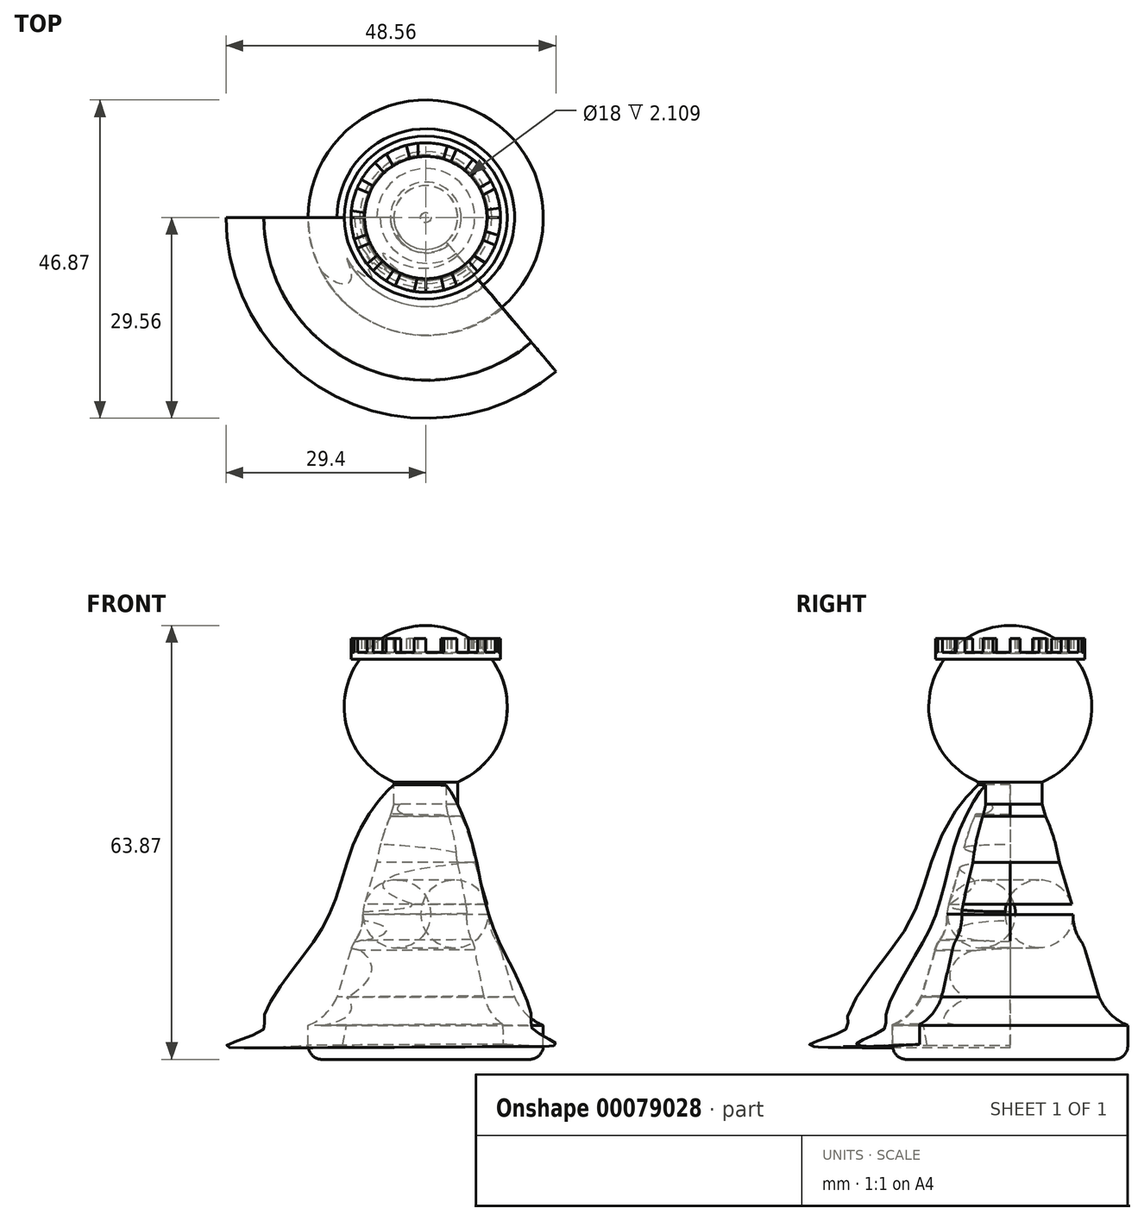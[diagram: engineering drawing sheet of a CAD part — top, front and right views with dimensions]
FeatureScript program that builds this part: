
annotation { "Feature Type Name" : "Feature", "Feature Type Description" : "" }
export const myFeature = defineFeature(function(context is Context, id is Id, definition is map)
    precondition{}
    {
        {
            var Q0;
            Q0=qCreatedBy(makeId("Front.planeOp"),FACE);
            var sketch = newSketch(context, id + "F0", { "sketchPlane" : qUnion([Q0])});
            skArc(sketch, "E0", {"start": v(0, 32.95) * mm, "mid": v(-11.76, 23.35) * mm, "end": v(-4.7, 9.9) * mm});
            skLineSegment(sketch, "E1", {"start": v(-4.7, 9.9) * mm, "end": v(-4.7, 6.63) * mm});
            skLineSegment(sketch, "E2", {"start": v(-4.7, 6.63) * mm, "end": v(-5.22, 4.84) * mm});
            skLineSegment(sketch, "E3", {"start": v(-14.3, -25.92) * mm, "end": v(0, -25.92) * mm});
            skLineSegment(sketch, "E4", {"start": v(0, -25.92) * mm, "end": v(0, 8.95) * mm});
            skArc(sketch, "E5", {"start": v(-10.38, -13.48) * mm, "mid": v(-9.51, -11.62) * mm, "end": v(-9.24, -9.6) * mm});
            skLineSegment(sketch, "E6.trimOffspring", {"start": v(-11.03, -14.85) * mm, "end": v(-13.07, -21.75) * mm});
            skPoint(sketch, "E7.visualSharp", {"position": v(-9.28, -8.93) * mm});
            skArc(sketch, "E7.filletArc", {"start": v(-9.03, -8.08) * mm, "mid": v(-9.2, -8.83) * mm, "end": v(-9.24, -9.6) * mm});
            skPoint(sketch, "E8.visualSharp", {"position": v(-10.78, -14) * mm});
            skArc(sketch, "E8.filletArc", {"start": v(-10.38, -13.48) * mm, "mid": v(-10.76, -14.14) * mm, "end": v(-11.03, -14.85) * mm});
            skLineSegment(sketch, "E9", {"start": v(0, 32.95) * mm, "end": v(0, 8.95) * mm});
            skArc(sketch, "E10", {"start": v(-17.3, -25.92) * mm, "mid": v(-14.78, -24.25) * mm, "end": v(-13.07, -21.75) * mm});
            skLineSegment(sketch, "E11", {"start": v(-17.3, -25.92) * mm, "end": v(-14.3, -25.92) * mm});
            skArc(sketch, "E12", {"start": v(-5.22, 4.84) * mm, "mid": v(-6.44, 1.54) * mm, "end": v(-7.2, -1.9) * mm});
            skLineSegment(sketch, "E13.trimOffspring", {"start": v(-7.2, -1.9) * mm, "end": v(-9.03, -8.08) * mm});
            skSolve(sketch);
        }
        {
            var Q0;
            Q0 = qSketchRegion(id + "F0", true);
            var Q1;
            Q1=sQuery(id+"F0.wireOp",EDGE,"E9");
            revolve(context, id + "F1", {"entities" : qUnion([Q0]), "axis" : qUnion([Q1]), "revolveType" : RevolveType.FULL});
        }
        {
            var Q0;
            Q0=qCreatedBy(makeId("Top.planeOp"),FACE);
            cPlane(context, id + "F2", {"entities" : qUnion([Q0]), "cplaneType" : CPlaneType.OFFSET, "offset" : 28 * mm, "width" : 150 * mm, "height" : 150 * mm});
        }
        {
            var Q0;
            Q0=qCreatedBy(id+"F2.planeOp",FACE);
            var sketch = newSketch(context, id + "F3", { "sketchPlane" : qUnion([Q0])});
            skCircle(sketch, "E14", {"center": v(0, 0) * mm, "radius": 11 * mm});
            skCircle(sketch, "E15", {"center": v(0, 0) * mm, "radius": 9 * mm});
            skLineSegment(sketch, "E16", {"start": v(-2.83, 10.63) * mm, "end": v(-2.32, 8.7) * mm});
            skLineSegment(sketch, "E17", {"start": v(-4.8, 7.61) * mm, "end": v(-5.8, 9.35) * mm});
            skLineSegment(sketch, "E18", {"start": v(-7.73, 4.6) * mm, "end": v(-9.47, 5.6) * mm});
            skLineSegment(sketch, "E19", {"start": v(9, 0) * mm, "end": v(11, 0) * mm});
            skLineSegment(sketch, "E20", {"start": v(6.29, -6.44) * mm, "end": v(7.6, -7.95) * mm});
            skLineSegment(sketch, "E21", {"start": v(3.82, -8.15) * mm, "end": v(4.57, -10) * mm});
            skLineSegment(sketch, "E22", {"start": v(2.25, -8.71) * mm, "end": v(2.66, -10.67) * mm});
            skLineSegment(sketch, "E23", {"start": v(0, -9) * mm, "end": v(0, -11) * mm});
            skLineSegment(sketch, "E24", {"start": v(-1.12, 10.94) * mm, "end": v(-1.12, 8.93) * mm});
            skLineSegment(sketch, "E25", {"start": v(-7.47, 8.08) * mm, "end": v(-6.1, 6.62) * mm});
            skLineSegment(sketch, "E26", {"start": v(-1.28, -8.9) * mm, "end": v(-1.7, -10.87) * mm});
            skLineSegment(sketch, "E27", {"start": v(-3.65, -8.22) * mm, "end": v(-4.5, -10.04) * mm});
            skLineSegment(sketch, "E28", {"start": v(-4.69, -7.68) * mm, "end": v(-5.84, -9.32) * mm});
            skLineSegment(sketch, "E29", {"start": v(-6.34, -6.39) * mm, "end": v(-7.74, -7.82) * mm});
            skLineSegment(sketch, "E30", {"start": v(-7.08, -5.55) * mm, "end": v(-8.66, -6.78) * mm});
            skLineSegment(sketch, "E31", {"start": v(-8.19, -3.74) * mm, "end": v(-10.03, -4.52) * mm});
            skLineSegment(sketch, "E32", {"start": v(-8.65, -2.5) * mm, "end": v(-10.54, -3.15) * mm});
            skLineSegment(sketch, "E33", {"start": v(-9, 0) * mm, "end": v(-11, 0) * mm});
            skLineSegment(sketch, "E34", {"start": v(-8.97, 0.69) * mm, "end": v(-10.95, 1.02) * mm});
            skLineSegment(sketch, "E35", {"start": v(-8.26, 3.57) * mm, "end": v(-10.12, 4.3) * mm});
            skLineSegment(sketch, "E36", {"start": v(7.07, -5.56) * mm, "end": v(8.75, -6.67) * mm});
            skLineSegment(sketch, "E37", {"start": v(8.37, -3.32) * mm, "end": v(10.23, -4.04) * mm});
            skLineSegment(sketch, "E38", {"start": v(8.77, -2.02) * mm, "end": v(10.7, -2.59) * mm});
            skLineSegment(sketch, "E39", {"start": v(8.93, 1.13) * mm, "end": v(10.9, 1.42) * mm});
            skLineSegment(sketch, "E40", {"start": v(8.38, 3.28) * mm, "end": v(10.15, 4.23) * mm});
            skLineSegment(sketch, "E41", {"start": v(7.86, 4.38) * mm, "end": v(9.62, 5.33) * mm});
            skLineSegment(sketch, "E42", {"start": v(6.65, 6.07) * mm, "end": v(8.07, 7.48) * mm});
            skLineSegment(sketch, "E43", {"start": v(5.74, 6.93) * mm, "end": v(6.92, 8.55) * mm});
            skLineSegment(sketch, "E44", {"start": v(3.67, 8.22) * mm, "end": v(4.51, 10.03) * mm});
            skLineSegment(sketch, "E45", {"start": v(2.58, 8.62) * mm, "end": v(3.2, 10.52) * mm});
            skSolve(sketch);
        }
        {
            var Q0;
            {var subQ0=sQuery(id+"F3.wireOp",EDGE,"E18");Q0=makeQuery(id+"F3.imprint","IMPRINT",FACE,{"disambiguationData":[TD([[makeQuery(id+"F3.imprint","IMPRINT",EDGE,{"derivedFrom":subQ0}),1.0]])]});}
            var Q1;
            {var subQ0=sQuery(id+"F3.wireOp",EDGE,"E17");Q1=makeQuery(id+"F3.imprint","IMPRINT",FACE,{"disambiguationData":[TD([[makeQuery(id+"F3.imprint","IMPRINT",EDGE,{"derivedFrom":subQ0}),1.0]])]});}
            var Q2;
            {var subQ0=sQuery(id+"F3.wireOp",EDGE,"E16");Q2=makeQuery(id+"F3.imprint","IMPRINT",FACE,{"disambiguationData":[TD([[makeQuery(id+"F3.imprint","IMPRINT",EDGE,{"derivedFrom":subQ0}),1.0]])]});}
            var Q3;
            {var subQ0=sQuery(id+"F3.wireOp",EDGE,"E44");Q3=makeQuery(id+"F3.imprint","IMPRINT",FACE,{"disambiguationData":[TD([[makeQuery(id+"F3.imprint","IMPRINT",EDGE,{"derivedFrom":subQ0}),1.0]])]});}
            var Q4;
            {var subQ0=sQuery(id+"F3.wireOp",EDGE,"E42");Q4=makeQuery(id+"F3.imprint","IMPRINT",FACE,{"disambiguationData":[TD([[makeQuery(id+"F3.imprint","IMPRINT",EDGE,{"derivedFrom":subQ0}),1.0]])]});}
            var Q5;
            {var subQ0=sQuery(id+"F3.wireOp",EDGE,"E40");Q5=makeQuery(id+"F3.imprint","IMPRINT",FACE,{"disambiguationData":[TD([[makeQuery(id+"F3.imprint","IMPRINT",EDGE,{"derivedFrom":subQ0}),1.0]])]});}
            var Q6;
            {var subQ0=sQuery(id+"F3.wireOp",EDGE,"E19");Q6=makeQuery(id+"F3.imprint","IMPRINT",FACE,{"disambiguationData":[TD([[makeQuery(id+"F3.imprint","IMPRINT",EDGE,{"derivedFrom":subQ0}),1.0]])]});}
            var Q7;
            {var subQ0=sQuery(id+"F3.wireOp",EDGE,"E37");Q7=makeQuery(id+"F3.imprint","IMPRINT",FACE,{"disambiguationData":[TD([[makeQuery(id+"F3.imprint","IMPRINT",EDGE,{"derivedFrom":subQ0}),1.0]])]});}
            var Q8;
            {var subQ0=sQuery(id+"F3.wireOp",EDGE,"E20");Q8=makeQuery(id+"F3.imprint","IMPRINT",FACE,{"disambiguationData":[TD([[makeQuery(id+"F3.imprint","IMPRINT",EDGE,{"derivedFrom":subQ0}),1.0]])]});}
            var Q9;
            {var subQ0=sQuery(id+"F3.wireOp",EDGE,"E21");Q9=makeQuery(id+"F3.imprint","IMPRINT",FACE,{"disambiguationData":[TD([[makeQuery(id+"F3.imprint","IMPRINT",EDGE,{"derivedFrom":subQ0}),-1.0]])]});}
            var Q10;
            {var subQ0=sQuery(id+"F3.wireOp",EDGE,"E23");Q10=makeQuery(id+"F3.imprint","IMPRINT",FACE,{"disambiguationData":[TD([[makeQuery(id+"F3.imprint","IMPRINT",EDGE,{"derivedFrom":subQ0}),-1.0]])]});}
            var Q11;
            {var subQ0=sQuery(id+"F3.wireOp",EDGE,"E27");Q11=makeQuery(id+"F3.imprint","IMPRINT",FACE,{"disambiguationData":[TD([[makeQuery(id+"F3.imprint","IMPRINT",EDGE,{"derivedFrom":subQ0}),-1.0]])]});}
            var Q12;
            {var subQ0=sQuery(id+"F3.wireOp",EDGE,"E29");Q12=makeQuery(id+"F3.imprint","IMPRINT",FACE,{"disambiguationData":[TD([[makeQuery(id+"F3.imprint","IMPRINT",EDGE,{"derivedFrom":subQ0}),-1.0]])]});}
            var Q13;
            {var subQ0=sQuery(id+"F3.wireOp",EDGE,"E31");Q13=makeQuery(id+"F3.imprint","IMPRINT",FACE,{"disambiguationData":[TD([[makeQuery(id+"F3.imprint","IMPRINT",EDGE,{"derivedFrom":subQ0}),-1.0]])]});}
            var Q14;
            {var subQ0=sQuery(id+"F3.wireOp",EDGE,"E33");Q14=makeQuery(id+"F3.imprint","IMPRINT",FACE,{"disambiguationData":[TD([[makeQuery(id+"F3.imprint","IMPRINT",EDGE,{"derivedFrom":subQ0}),-1.0]])]});}
            extrude(context, id + "F4", {"entities" : qUnion([Q0, Q1, Q2, Q3, Q4, Q5, Q6, Q7, Q8, Q9, Q10, Q11, Q12, Q13, Q14]), "operationType" : NewBodyOperationType.ADD, "depth" : 3 * mm});
        }
        {
            var Q0;
            {var subQ0=sQuery(id+"F3.wireOp",EDGE,"E16");Q0=makeQuery(id+"F3.imprint","IMPRINT",FACE,{"disambiguationData":[TD([[makeQuery(id+"F3.imprint","IMPRINT",EDGE,{"derivedFrom":subQ0}),-1.0]])]});}
            var Q1;
            {var subQ0=sQuery(id+"F3.wireOp",EDGE,"E18");Q1=makeQuery(id+"F3.imprint","IMPRINT",FACE,{"disambiguationData":[TD([[makeQuery(id+"F3.imprint","IMPRINT",EDGE,{"derivedFrom":subQ0}),-1.0]])]});}
            var Q2;
            {var subQ0=sQuery(id+"F3.wireOp",EDGE,"E34");Q2=makeQuery(id+"F3.imprint","IMPRINT",FACE,{"disambiguationData":[TD([[makeQuery(id+"F3.imprint","IMPRINT",EDGE,{"derivedFrom":subQ0}),-1.0]])]});}
            var Q3;
            {var subQ0=sQuery(id+"F3.wireOp",EDGE,"E32");Q3=makeQuery(id+"F3.imprint","IMPRINT",FACE,{"disambiguationData":[TD([[makeQuery(id+"F3.imprint","IMPRINT",EDGE,{"derivedFrom":subQ0}),-1.0]])]});}
            var Q4;
            {var subQ0=sQuery(id+"F3.wireOp",EDGE,"E30");Q4=makeQuery(id+"F3.imprint","IMPRINT",FACE,{"disambiguationData":[TD([[makeQuery(id+"F3.imprint","IMPRINT",EDGE,{"derivedFrom":subQ0}),-1.0]])]});}
            var Q5;
            {var subQ0=sQuery(id+"F3.wireOp",EDGE,"E28");Q5=makeQuery(id+"F3.imprint","IMPRINT",FACE,{"disambiguationData":[TD([[makeQuery(id+"F3.imprint","IMPRINT",EDGE,{"derivedFrom":subQ0}),-1.0]])]});}
            var Q6;
            {var subQ0=sQuery(id+"F3.wireOp",EDGE,"E26");Q6=makeQuery(id+"F3.imprint","IMPRINT",FACE,{"disambiguationData":[TD([[makeQuery(id+"F3.imprint","IMPRINT",EDGE,{"derivedFrom":subQ0}),-1.0]])]});}
            var Q7;
            {var subQ0=sQuery(id+"F3.wireOp",EDGE,"E22");Q7=makeQuery(id+"F3.imprint","IMPRINT",FACE,{"disambiguationData":[TD([[makeQuery(id+"F3.imprint","IMPRINT",EDGE,{"derivedFrom":subQ0}),-1.0]])]});}
            var Q8;
            {var subQ0=sQuery(id+"F3.wireOp",EDGE,"E20");Q8=makeQuery(id+"F3.imprint","IMPRINT",FACE,{"disambiguationData":[TD([[makeQuery(id+"F3.imprint","IMPRINT",EDGE,{"derivedFrom":subQ0}),-1.0]])]});}
            var Q9;
            {var subQ0=sQuery(id+"F3.wireOp",EDGE,"E36");Q9=makeQuery(id+"F3.imprint","IMPRINT",FACE,{"disambiguationData":[TD([[makeQuery(id+"F3.imprint","IMPRINT",EDGE,{"derivedFrom":subQ0}),1.0]])]});}
            var Q10;
            {var subQ0=sQuery(id+"F3.wireOp",EDGE,"E19");Q10=makeQuery(id+"F3.imprint","IMPRINT",FACE,{"disambiguationData":[TD([[makeQuery(id+"F3.imprint","IMPRINT",EDGE,{"derivedFrom":subQ0}),-1.0]])]});}
            var Q11;
            {var subQ0=sQuery(id+"F3.wireOp",EDGE,"E39");Q11=makeQuery(id+"F3.imprint","IMPRINT",FACE,{"disambiguationData":[TD([[makeQuery(id+"F3.imprint","IMPRINT",EDGE,{"derivedFrom":subQ0}),1.0]])]});}
            var Q12;
            {var subQ0=sQuery(id+"F3.wireOp",EDGE,"E41");Q12=makeQuery(id+"F3.imprint","IMPRINT",FACE,{"disambiguationData":[TD([[makeQuery(id+"F3.imprint","IMPRINT",EDGE,{"derivedFrom":subQ0}),1.0]])]});}
            var Q13;
            {var subQ0=sQuery(id+"F3.wireOp",EDGE,"E43");Q13=makeQuery(id+"F3.imprint","IMPRINT",FACE,{"disambiguationData":[TD([[makeQuery(id+"F3.imprint","IMPRINT",EDGE,{"derivedFrom":subQ0}),1.0]])]});}
            var Q14;
            {var subQ0=sQuery(id+"F3.wireOp",EDGE,"E24");Q14=makeQuery(id+"F3.imprint","IMPRINT",FACE,{"disambiguationData":[TD([[makeQuery(id+"F3.imprint","IMPRINT",EDGE,{"derivedFrom":subQ0}),1.0]])]});}
            extrude(context, id + "F5", {"entities" : qUnion([Q0, Q1, Q2, Q3, Q4, Q5, Q6, Q7, Q8, Q9, Q10, Q11, Q12, Q13, Q14]), "operationType" : NewBodyOperationType.ADD, "depth" : 1 * mm});
        }
        {
            var Q0;
            Q0=makeQuery(id+"F1.opRevolve","SWEPT_FACE",FACE,{"disambiguationData":[OSD([sQuery(id+"F0.wireOp",EDGE,"E3"),sQuery(id+"F0.wireOp",EDGE,"E11")])]});
            extrude(context, id + "F6", {"entities" : qUnion([Q0]), "operationType" : NewBodyOperationType.ADD, "depth" : 5 * mm});
        }
        {
            var Q0;
            Q0=makeQuery(id+"F6.opExtrude","CAP_EDGE",EDGE,{"disambiguationData":[OSD([sQuery(id+"F0.wireOp",EDGE,"E10"),sQuery(id+"F0.wireOp",EDGE,"E11")])],"isStart":false});
            fillet(context, id + "F7", {"entities" : qUnion([Q0]), "radius" : 2 * mm, "tangentPropagation" : true, "allowEdgeOverflow" : false});
        }
        {
            var Q0;
            Q0=qCreatedBy(makeId("Front.planeOp"),FACE);
            var sketch = newSketch(context, id + "F8", { "sketchPlane" : qUnion([Q0])});
            skArc(sketch, "E46", {"start": v(-5.12, 5.2) * mm, "mid": v(-4.39, 7.73) * mm, "end": v(-3.7, 10.28) * mm});
            skArc(sketch, "E47", {"start": v(-5.12, 5.2) * mm, "mid": v(-6.4, 1.7) * mm, "end": v(-7.18, -1.94) * mm});
            skArc(sketch, "E48", {"start": v(-7.18, -1.94) * mm, "mid": v(-8.12, -5) * mm, "end": v(-8.99, -8.09) * mm});
            skArc(sketch, "E49", {"start": v(-8.99, -8.09) * mm, "mid": v(-9.17, -8.83) * mm, "end": v(-9.28, -9.59) * mm});
            skArc(sketch, "E50", {"start": v(-10.32, -13.4) * mm, "mid": v(-9.47, -11.59) * mm, "end": v(-9.28, -9.59) * mm});
            skArc(sketch, "E51", {"start": v(-10.32, -13.4) * mm, "mid": v(-10.76, -14.12) * mm, "end": v(-11.03, -14.9) * mm});
            skArc(sketch, "E52", {"start": v(-13.05, -21.74) * mm, "mid": v(-12.02, -18.32) * mm, "end": v(-11.03, -14.9) * mm});
            skPoint(sketch, "E53.1.internal.orphan", {"position": v(-4.47, 10.28) * mm});
            skArc(sketch, "E54", {"start": v(-17.26, -25.92) * mm, "mid": v(-14.73, -24.26) * mm, "end": v(-13.05, -21.74) * mm});
            skLineSegment(sketch, "E55", {"start": v(-17.26, -25.92) * mm, "end": v(-17.26, -28.86) * mm});
            skFitSpline(sketch, "E56", {"points": [v(-3.7, 10.28) * mm, v(-5.5, 8.76) * mm, v(-10, 2.26) * mm, v(-13.9, -8.94) * mm, v(-18.88, -16.76) * mm, v(-23.85, -24.98) * mm, v(-23.9, -26.5) * mm, v(-29.33, -28.86) * mm, v(-17.26, -28.86) * mm], "startDerivative": vector(-22.26, -16.74) * mm, "endDerivative": vector(116.82, 6.37) * mm});
            skLineSegment(sketch, "E57", {"start": v(0, 0) * mm, "end": v(-0.17, 30.19) * mm});
            skSolve(sketch);
        }
        {
            var Q0;
            Q0=makeQuery(id+"F8.imprint","IMPRINT",FACE,{"disambiguationData":[TD([[makeQuery(id+"F8.imprint","IMPRINT",EDGE,{"derivedFrom":sQuery(id+"F8.wireOp",EDGE,"E46")}),1.0]])]});
            var Q1;
            Q1=sQuery(id+"F8.wireOp",EDGE,"E57");
            revolve(context, id + "F9", {"operationType" : NewBodyOperationType.ADD, "entities" : qUnion([Q0]), "axis" : qUnion([Q1]), "revolveType" : RevolveType.ONE_DIRECTION, "angle" : 130 * degree});
        }
    });
